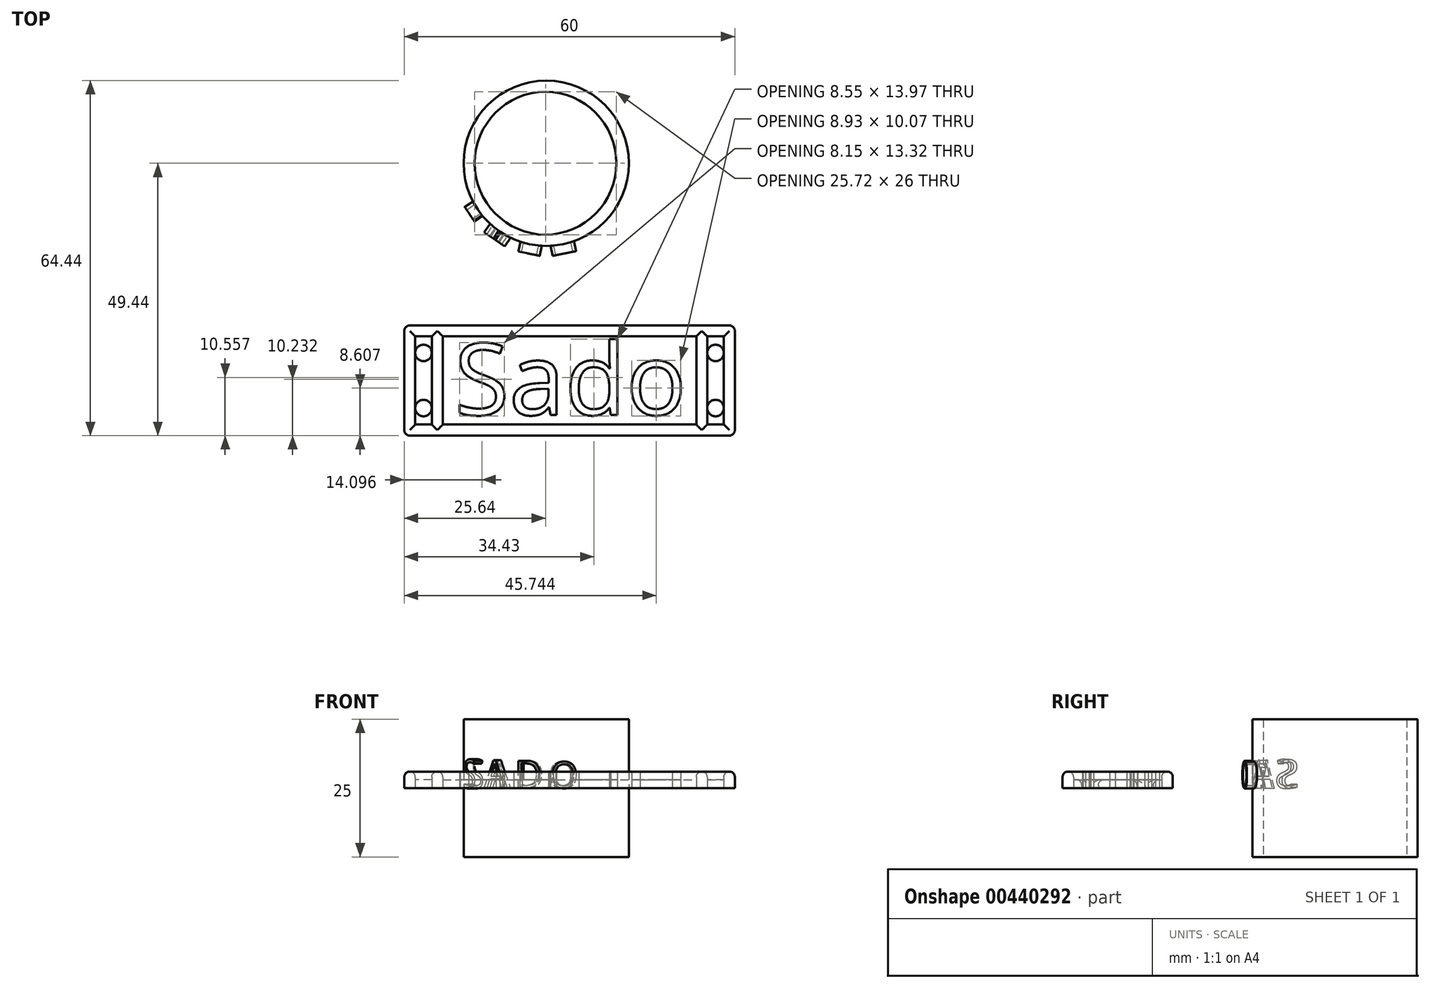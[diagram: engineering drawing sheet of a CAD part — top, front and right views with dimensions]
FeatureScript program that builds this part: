
annotation { "Feature Type Name" : "Feature", "Feature Type Description" : "" }
export const myFeature = defineFeature(function(context is Context, id is Id, definition is map)
    precondition{}
    {
        {
            var Q0;
            Q0=qCreatedBy(makeId("Top.planeOp"),FACE);
            var sketch = newSketch(context, id + "F0", { "sketchPlane" : qUnion([Q0])});
            skLineSegment(sketch, "E0", {"start": v(0, -15) * mm, "end": v(5.74, -13.86) * mm});
            skLineSegment(sketch, "E1", {"start": v(5.74, -13.86) * mm, "end": v(10.6, -10.6) * mm});
            skLineSegment(sketch, "E2", {"start": v(10.6, -10.6) * mm, "end": v(13.86, -5.74) * mm});
            skLineSegment(sketch, "E3", {"start": v(13.86, -5.74) * mm, "end": v(15, 0) * mm});
            skLineSegment(sketch, "E4", {"start": v(15, 0) * mm, "end": v(13.86, 5.74) * mm});
            skLineSegment(sketch, "E5", {"start": v(13.86, 5.74) * mm, "end": v(10.6, 10.6) * mm});
            skLineSegment(sketch, "E6", {"start": v(10.6, 10.6) * mm, "end": v(5.74, 13.86) * mm});
            skLineSegment(sketch, "E7", {"start": v(5.74, 13.86) * mm, "end": v(0, 15) * mm});
            skLineSegment(sketch, "E8", {"start": v(0, 15) * mm, "end": v(-5.74, 13.86) * mm});
            skLineSegment(sketch, "E9", {"start": v(-5.74, 13.86) * mm, "end": v(-10.6, 10.6) * mm});
            skLineSegment(sketch, "E10", {"start": v(-10.6, 10.6) * mm, "end": v(-13.86, 5.74) * mm});
            skLineSegment(sketch, "E11", {"start": v(-13.86, 5.74) * mm, "end": v(-15, 0) * mm});
            skLineSegment(sketch, "E12", {"start": v(-15, 0) * mm, "end": v(-13.86, -5.74) * mm});
            skLineSegment(sketch, "E13", {"start": v(-13.86, -5.74) * mm, "end": v(-10.6, -10.6) * mm});
            skLineSegment(sketch, "E14", {"start": v(-10.6, -10.6) * mm, "end": v(-5.74, -13.86) * mm});
            skLineSegment(sketch, "E15", {"start": v(-5.74, -13.86) * mm, "end": v(0, -15) * mm});
            skSolve(sketch);
        }
        {
            var Q0;
            Q0=qCreatedBy(makeId("Top.planeOp"),FACE);
            var sketch = newSketch(context, id + "F1", { "sketchPlane" : qUnion([Q0])});
            skCircle(sketch, "E16", {"center": v(0, 0) * mm, "radius": 15 * mm});
            skCircle(sketch, "E17.0", {"center": v(0, 0) * mm, "radius": 13 * mm});
            skSolve(sketch);
        }
        {
            var Q0;
            Q0=makeQuery(id+"F0.imprint","IMPRINT",FACE,{"disambiguationData":[TD([[makeQuery(id+"F0.imprint","IMPRINT",EDGE,{"derivedFrom":sQuery(id+"F0.wireOp",EDGE,"E0")}),1.0]])]});
            extrude(context, id + "F2", {"entities" : qUnion([Q0]), "endBound" : BoundingType.SYMMETRIC, "depth" : 25 * mm, "offsetDistance" : 25 * mm});
        }
        {
            var Q0;
            Q0=makeQuery(id+"F2.opExtrude","SWEPT_FACE",FACE,{"disambiguationData":[OSD([sQuery(id+"F0.wireOp",EDGE,"E13")])]});
            var sketch = newSketch(context, id + "F3", { "sketchPlane" : qUnion([Q0])});
            skText(sketch, "E18", { "text": "S", "fontName": "OpenSans-Regular.ttf"});
            const initialGuessF3  = {"E18": [-0.00204, 0, 1, 0, 0.0052]};
            skSetInitialGuess(sketch, initialGuessF3);
            skSolve(sketch);
        }
        {
            var Q0;
            Q0=makeQuery(id+"F3.imprint","IMPRINT",FACE,{"disambiguationData":[TD([[makeQuery(id+"F3.imprint","IMPRINT",EDGE,{"derivedFrom":sQuery(id+"F3.wireOp",EDGE,"E18.sketch_text.stroke-0")}),-1.0]])]});
            extrude(context, id + "F4", {"entities" : qUnion([Q0]), "operationType" : NewBodyOperationType.ADD, "depth" : 2 * mm, "offsetDistance" : 25 * mm});
        }
        {
            var Q0;
            Q0=makeQuery(id+"F2.opExtrude","SWEPT_FACE",FACE,{"disambiguationData":[OSD([sQuery(id+"F0.wireOp",EDGE,"E14")])]});
            var sketch = newSketch(context, id + "F5", { "sketchPlane" : qUnion([Q0])});
            skText(sketch, "E19", { "text": "A", "fontName": "OpenSans-Regular.ttf"});
            skPoint(sketch, "E19.secondSnap0", {"position": v(-0.97, 0) * mm});
            const initialGuessF5  = {"E19": [-0.00237, 0, 1, 0, 0.00511]};
            skSetInitialGuess(sketch, initialGuessF5);
            skSolve(sketch);
        }
        {
            var Q0;
            Q0 = qSketchRegion(id + "F5", true);
            extrude(context, id + "F6", {"entities" : qUnion([Q0]), "operationType" : NewBodyOperationType.ADD, "depth" : 2 * mm, "offsetDistance" : 25 * mm});
        }
        {
            var Q0;
            Q0=makeQuery(id+"F2.opExtrude","SWEPT_FACE",FACE,{"disambiguationData":[OSD([sQuery(id+"F0.wireOp",EDGE,"E15")])]});
            var sketch = newSketch(context, id + "F7", { "sketchPlane" : qUnion([Q0])});
            skText(sketch, "E20", { "text": "D", "fontName": "OpenSans-Regular.ttf"});
            const initialGuessF7  = {"E20": [-0.00251, 0, 1, 0, 0.00501]};
            skSetInitialGuess(sketch, initialGuessF7);
            skSolve(sketch);
        }
        {
            var Q0;
            Q0 = qSketchRegion(id + "F7", true);
            extrude(context, id + "F8", {"entities" : qUnion([Q0]), "operationType" : NewBodyOperationType.ADD, "depth" : 2 * mm, "offsetDistance" : 25 * mm});
        }
        {
            var Q0;
            Q0=makeQuery(id+"F2.opExtrude","SWEPT_FACE",FACE,{"disambiguationData":[OSD([sQuery(id+"F0.wireOp",EDGE,"E0")])]});
            var sketch = newSketch(context, id + "F9", { "sketchPlane" : qUnion([Q0])});
            skText(sketch, "E21", { "text": "O", "fontName": "OpenSans-Regular.ttf"});
            const initialGuessF9  = {"E21": [-0.00258, 0, 1, 0, 0.00478]};
            skSetInitialGuess(sketch, initialGuessF9);
            skSolve(sketch);
        }
        {
            var Q0;
            Q0=makeQuery(id+"F9.imprint","IMPRINT",FACE,{"disambiguationData":[TD([[makeQuery(id+"F9.imprint","IMPRINT",EDGE,{"derivedFrom":sQuery(id+"F9.wireOp",EDGE,"E21.sketch_text.stroke-0")}),-1.0]])]});
            extrude(context, id + "F10", {"entities" : qUnion([Q0]), "operationType" : NewBodyOperationType.ADD, "depth" : 2 * mm, "offsetDistance" : 25 * mm});
        }
        {
            var Q0;
            Q0=makeQuery(id+"F1.imprint","IMPRINT",FACE,{"disambiguationData":[TD([[makeQuery(id+"F1.imprint","IMPRINT",EDGE,{"derivedFrom":sQuery(id+"F1.wireOp",EDGE,"E16")}),1.0]])]});
            extrude(context, id + "F11", {"entities" : qUnion([Q0]), "operationType" : NewBodyOperationType.ADD, "endBound" : BoundingType.SYMMETRIC, "depth" : 25 * mm, "offsetDistance" : 25 * mm});
        }
        {
            var Q0;
            Q0=makeQuery(id+"F11.boolean.opBoolean","MERGE",FACE,{"derivedFrom":[makeQuery(id+"F2.opExtrude","CAP_FACE",FACE,{"disambiguationData":[OSD([sQuery(id+"F0.wireOp",EDGE,"E0"),sQuery(id+"F0.wireOp",EDGE,"E1"),sQuery(id+"F0.wireOp",EDGE,"E2"),sQuery(id+"F0.wireOp",EDGE,"E3"),sQuery(id+"F0.wireOp",EDGE,"E4"),sQuery(id+"F0.wireOp",EDGE,"E5"),sQuery(id+"F0.wireOp",EDGE,"E6"),sQuery(id+"F0.wireOp",EDGE,"E7"),sQuery(id+"F0.wireOp",EDGE,"E8"),sQuery(id+"F0.wireOp",EDGE,"E9"),sQuery(id+"F0.wireOp",EDGE,"E10"),sQuery(id+"F0.wireOp",EDGE,"E11"),sQuery(id+"F0.wireOp",EDGE,"E12"),sQuery(id+"F0.wireOp",EDGE,"E13"),sQuery(id+"F0.wireOp",EDGE,"E14"),sQuery(id+"F0.wireOp",EDGE,"E15")])],"isStart":true}),makeQuery(id+"F11.opExtrude","CAP_FACE",FACE,{"disambiguationData":[OSD([sQuery(id+"F1.wireOp",EDGE,"E16")])],"isStart":true})]});
            var sketch = newSketch(context, id + "F12", { "sketchPlane" : qUnion([Q0])});
            skCircle(sketch, "E22", {"center": v(-0.28, 0) * mm, "radius": 13 * mm});
            skSolve(sketch);
        }
        {
            var Q0;
            Q0=makeQuery(id+"F12.imprint","IMPRINT",FACE,{"disambiguationData":[TD([[makeQuery(id+"F12.imprint","IMPRINT",EDGE,{"derivedFrom":sQuery(id+"F12.wireOp",EDGE,"E22")}),1.0]])]});
            extrude(context, id + "F13", {"entities" : qUnion([Q0]), "operationType" : NewBodyOperationType.REMOVE, "oppositeDirection" : true, "depth" : 70 * mm, "offsetDistance" : 25 * mm});
        }
        {
            var Q0;
            Q0 = qSketchRegion(id + "F1", true);
            extrude(context, id + "F14", {"entities" : qUnion([Q0]), "operationType" : NewBodyOperationType.ADD, "endBound" : BoundingType.SYMMETRIC, "depth" : 25 * mm, "offsetDistance" : 25 * mm});
        }
        {
            var Q0;
            Q0=qCreatedBy(makeId("Top.planeOp"),FACE);
            var sketch = newSketch(context, id + "F15", { "sketchPlane" : qUnion([Q0])});
            skLineSegment(sketch, "E23", {"start": v(-20.78, -29.44) * mm, "end": v(-20.78, -49.44) * mm});
            skLineSegment(sketch, "E24", {"start": v(-20.78, -49.44) * mm, "end": v(29.22, -49.44) * mm});
            skLineSegment(sketch, "E25", {"start": v(29.22, -47.44) * mm, "end": v(29.22, -31.44) * mm});
            skLineSegment(sketch, "E26", {"start": v(29.22, -29.44) * mm, "end": v(-20.78, -29.44) * mm});
            skText(sketch, "E27", { "text": "Sado", "fontName": "OpenSans-Regular.ttf"});
            skLineSegment(sketch, "E28.0", {"start": v(27.22, -47.44) * mm, "end": v(27.22, -31.44) * mm});
            skLineSegment(sketch, "E29.0", {"start": v(27.22, -31.44) * mm, "end": v(-18.78, -31.44) * mm});
            skLineSegment(sketch, "E30.0", {"start": v(-18.78, -47.44) * mm, "end": v(27.22, -47.44) * mm});
            skLineSegment(sketch, "E31.0", {"start": v(-18.78, -31.44) * mm, "end": v(-18.78, -47.44) * mm});
            skLineSegment(sketch, "E32.0", {"start": v(34.22, -49.44) * mm, "end": v(34.22, -29.44) * mm});
            skLineSegment(sketch, "E33", {"start": v(29.22, -49.44) * mm, "end": v(34.22, -49.44) * mm});
            skLineSegment(sketch, "E34", {"start": v(29.22, -29.44) * mm, "end": v(34.22, -29.44) * mm});
            skCircle(sketch, "E35", {"center": v(30.72, -34.44) * mm, "radius": 1.5 * mm});
            skCircle(sketch, "E36.MirrorC", {"center": v(30.72, -44.44) * mm, "radius": 1.5 * mm});
            skLineSegment(sketch, "E37.0", {"start": v(29.22, -31.44) * mm, "end": v(32.22, -31.44) * mm});
            skLineSegment(sketch, "E38.0", {"start": v(29.22, -47.44) * mm, "end": v(32.22, -47.44) * mm});
            skLineSegment(sketch, "E39.0", {"start": v(32.22, -47.44) * mm, "end": v(32.22, -31.44) * mm});
            skLineSegment(sketch, "E40.MirrorCS", {"start": v(-20.78, -31.44) * mm, "end": v(-23.78, -31.44) * mm});
            skLineSegment(sketch, "E41.MirrorCS", {"start": v(-20.78, -47.44) * mm, "end": v(-23.78, -47.44) * mm});
            skCircle(sketch, "E42.MirrorC", {"center": v(-22.28, -34.44) * mm, "radius": 1.5 * mm});
            skCircle(sketch, "E43.MirrorC", {"center": v(-22.28, -44.44) * mm, "radius": 1.5 * mm});
            skLineSegment(sketch, "E44.MirrorCS", {"start": v(-23.78, -47.44) * mm, "end": v(-23.78, -31.44) * mm});
            skLineSegment(sketch, "E45.MirrorCS", {"start": v(-20.78, -49.44) * mm, "end": v(-25.78, -49.44) * mm});
            skLineSegment(sketch, "E46.MirrorCS", {"start": v(-20.78, -29.44) * mm, "end": v(-25.78, -29.44) * mm});
            skLineSegment(sketch, "E47.MirrorCS", {"start": v(-25.78, -49.44) * mm, "end": v(-25.78, -29.44) * mm});
            const initialGuessF15  = {"E27": [-0.0167, -0.04569, 1, 0, 0.01307]};
            skSetInitialGuess(sketch, initialGuessF15);
            skSolve(sketch);
        }
        {
            var Q0;
            Q0 = qSketchRegion(id + "F15", true);
            var Q1;
            Q1=makeQuery(id+"F15.imprint","IMPRINT",FACE,{"disambiguationData":[TD([[makeQuery(id+"F15.imprint","IMPRINT",EDGE,{"derivedFrom":sQuery(id+"F15.wireOp",EDGE,"E27.sketch_text.stroke-76")}),-1.0]])]});
            var Q2;
            Q2=makeQuery(id+"F15.imprint","IMPRINT",FACE,{"disambiguationData":[TD([[makeQuery(id+"F15.imprint","IMPRINT",EDGE,{"derivedFrom":sQuery(id+"F15.wireOp",EDGE,"E27.sketch_text.stroke-52")}),-1.0]])]});
            var Q3;
            Q3=makeQuery(id+"F15.imprint","IMPRINT",FACE,{"disambiguationData":[TD([[makeQuery(id+"F15.imprint","IMPRINT",EDGE,{"derivedFrom":sQuery(id+"F15.wireOp",EDGE,"E27.sketch_text.stroke-25")}),-1.0]])]});
            var Q4;
            Q4=makeQuery(id+"F15.imprint","IMPRINT",FACE,{"disambiguationData":[TD([[makeQuery(id+"F15.imprint","IMPRINT",EDGE,{"derivedFrom":sQuery(id+"F15.wireOp",EDGE,"E27.sketch_text.stroke-0")}),-1.0]])]});
            extrude(context, id + "F16", {"entities" : qUnion([Q0, Q1, Q2, Q3, Q4]), "depth" : 3 * mm, "offsetDistance" : 25 * mm});
        }
        {
            var Q0;
            Q0=makeQuery(id+"F15.imprint","IMPRINT",FACE,{"disambiguationData":[TD([[makeQuery(id+"F15.imprint","IMPRINT",EDGE,{"derivedFrom":sQuery(id+"F15.wireOp",EDGE,"E27.sketch_text.stroke-0")}),1.0]])]});
            var Q1;
            Q1=makeQuery(id+"F15.imprint","IMPRINT",FACE,{"disambiguationData":[TD([[makeQuery(id+"F15.imprint","IMPRINT",EDGE,{"derivedFrom":sQuery(id+"F15.wireOp",EDGE,"E27.sketch_text.stroke-85")}),1.0]])]});
            var Q2;
            {var subQ0=sQuery(id+"F15.wireOp",EDGE,"E36.MirrorC");var subQ1=sQuery(id+"F15.wireOp",EDGE,"E25");var subQ2=makeQuery(id+"F15.imprint","INTERSECT",VERTEX,{"derivedFrom":[subQ1,subQ0]});Q2=makeQuery(id+"F15.imprint","IMPRINT",FACE,{"disambiguationData":[TD([[makeQuery(id+"F15.imprint","IMPRINT",EDGE,{"disambiguationData":[TD([[subQ2,-1.0]])],"derivedFrom":subQ1}),-1.0]])]});}
            var Q3;
            {var subQ0=sQuery(id+"F15.wireOp",EDGE,"E37.0");Q3=makeQuery(id+"F15.imprint","IMPRINT",FACE,{"disambiguationData":[TD([[makeQuery(id+"F15.imprint","IMPRINT",EDGE,{"derivedFrom":subQ0}),-1.0]])]});}
            var Q4;
            {var subQ0=sQuery(id+"F15.wireOp",EDGE,"E38.0");Q4=makeQuery(id+"F15.imprint","IMPRINT",FACE,{"disambiguationData":[TD([[makeQuery(id+"F15.imprint","IMPRINT",EDGE,{"derivedFrom":subQ0}),1.0]])]});}
            var Q5;
            Q5=makeQuery(id+"F15.imprint","IMPRINT",FACE,{"disambiguationData":[TD([[makeQuery(id+"F15.imprint","IMPRINT",EDGE,{"derivedFrom":sQuery(id+"F15.wireOp",EDGE,"E27.sketch_text.stroke-67")}),1.0]])]});
            var Q6;
            Q6=makeQuery(id+"F15.imprint","IMPRINT",FACE,{"disambiguationData":[TD([[makeQuery(id+"F15.imprint","IMPRINT",EDGE,{"derivedFrom":sQuery(id+"F15.wireOp",EDGE,"E27.sketch_text.stroke-44")}),1.0]])]});
            var Q7;
            {var subQ0=sQuery(id+"F15.wireOp",EDGE,"E42.MirrorC");var subQ1=sQuery(id+"F15.wireOp",EDGE,"E23");var subQ2=makeQuery(id+"F15.imprint","INTERSECT",VERTEX,{"derivedFrom":[subQ1,subQ0]});Q7=makeQuery(id+"F15.imprint","IMPRINT",FACE,{"disambiguationData":[TD([[makeQuery(id+"F15.imprint","IMPRINT",EDGE,{"disambiguationData":[TD([[subQ2,-1.0]])],"derivedFrom":subQ1}),-1.0]])]});}
            var Q8;
            {var subQ0=sQuery(id+"F15.wireOp",EDGE,"E40.MirrorCS");Q8=makeQuery(id+"F15.imprint","IMPRINT",FACE,{"disambiguationData":[TD([[makeQuery(id+"F15.imprint","IMPRINT",EDGE,{"derivedFrom":subQ0}),1.0]])]});}
            var Q9;
            {var subQ0=sQuery(id+"F15.wireOp",EDGE,"E41.MirrorCS");Q9=makeQuery(id+"F15.imprint","IMPRINT",FACE,{"disambiguationData":[TD([[makeQuery(id+"F15.imprint","IMPRINT",EDGE,{"derivedFrom":subQ0}),-1.0]])]});}
            extrude(context, id + "F17", {"entities" : qUnion([Q0, Q1, Q2, Q3, Q4, Q5, Q6, Q7, Q8, Q9]), "depth" : 1.5 * mm, "offsetDistance" : 25 * mm});
        }
        {
            var Q0;
            Q0=makeQuery(id+"F16.opExtrude","CAP_FACE",FACE,{"disambiguationData":[OSD([sQuery(id+"F15.wireOp",EDGE,"E23"),sQuery(id+"F15.wireOp",EDGE,"E24"),sQuery(id+"F15.wireOp",EDGE,"E25"),sQuery(id+"F15.wireOp",EDGE,"E26"),sQuery(id+"F15.wireOp",EDGE,"E28.0"),sQuery(id+"F15.wireOp",EDGE,"E29.0"),sQuery(id+"F15.wireOp",EDGE,"E30.0"),sQuery(id+"F15.wireOp",EDGE,"E31.0"),sQuery(id+"F15.wireOp",EDGE,"E32.0"),sQuery(id+"F15.wireOp",EDGE,"E33"),sQuery(id+"F15.wireOp",EDGE,"E34"),sQuery(id+"F15.wireOp",EDGE,"E37.0"),sQuery(id+"F15.wireOp",EDGE,"E38.0"),sQuery(id+"F15.wireOp",EDGE,"E39.0"),sQuery(id+"F15.wireOp",EDGE,"E40.MirrorCS"),sQuery(id+"F15.wireOp",EDGE,"E41.MirrorCS"),sQuery(id+"F15.wireOp",EDGE,"E44.MirrorCS"),sQuery(id+"F15.wireOp",EDGE,"E45.MirrorCS"),sQuery(id+"F15.wireOp",EDGE,"E46.MirrorCS"),sQuery(id+"F15.wireOp",EDGE,"E47.MirrorCS")])],"isStart":false});
            var Q1;
            Q1=makeQuery(id+"F16.opExtrude","SWEPT_EDGE",EDGE,{"disambiguationData":[OSD([sQuery(id+"F15.wireOp",EDGE,"E45.MirrorCS"),sQuery(id+"F15.wireOp",EDGE,"E47.MirrorCS")])]});
            var Q2;
            Q2=makeQuery(id+"F16.opExtrude","SWEPT_EDGE",EDGE,{"disambiguationData":[OSD([sQuery(id+"F15.wireOp",EDGE,"E46.MirrorCS"),sQuery(id+"F15.wireOp",EDGE,"E47.MirrorCS")])]});
            var Q3;
            Q3=makeQuery(id+"F16.opExtrude","SWEPT_EDGE",EDGE,{"disambiguationData":[OSD([sQuery(id+"F15.wireOp",EDGE,"E32.0"),sQuery(id+"F15.wireOp",EDGE,"E34")])]});
            var Q4;
            Q4=makeQuery(id+"F16.opExtrude","SWEPT_EDGE",EDGE,{"disambiguationData":[OSD([sQuery(id+"F15.wireOp",EDGE,"E32.0"),sQuery(id+"F15.wireOp",EDGE,"E33")])]});
            var Q5;
            {var subQ0=sQuery(id+"F15.wireOp",EDGE,"E36.MirrorC");Q5=makeQuery(id+"F17.opExtrude","CAP_EDGE",EDGE,{"disambiguationData":[OSD([subQ0]),TDD([makeQuery(id+"F15.imprint","IMPRINT",EDGE,{"disambiguationData":[TD([[makeQuery(id+"F15.imprint","INTERSECT",VERTEX,{"derivedFrom":[sQuery(id+"F15.wireOp",EDGE,"E25"),subQ0]}),-1.0]])],"derivedFrom":subQ0})])],"isStart":false});}
            var Q6;
            {var subQ0=sQuery(id+"F15.wireOp",EDGE,"E35");Q6=makeQuery(id+"F17.opExtrude","CAP_EDGE",EDGE,{"disambiguationData":[OSD([subQ0]),TDD([makeQuery(id+"F15.imprint","IMPRINT",EDGE,{"disambiguationData":[TD([[makeQuery(id+"F15.imprint","INTERSECT",VERTEX,{"derivedFrom":[sQuery(id+"F15.wireOp",EDGE,"E25"),subQ0]}),-1.0]])],"derivedFrom":subQ0})])],"isStart":false});}
            var Q7;
            {var subQ0=sQuery(id+"F15.wireOp",EDGE,"E35");Q7=makeQuery(id+"F17.opExtrude","CAP_EDGE",EDGE,{"disambiguationData":[OSD([subQ0]),TDD([makeQuery(id+"F15.imprint","IMPRINT",EDGE,{"disambiguationData":[TD([[makeQuery(id+"F15.imprint","INTERSECT",VERTEX,{"derivedFrom":[sQuery(id+"F15.wireOp",EDGE,"E25"),subQ0]}),1.0]])],"derivedFrom":subQ0})])],"isStart":false});}
            var Q8;
            {var subQ0=sQuery(id+"F15.wireOp",EDGE,"E36.MirrorC");Q8=makeQuery(id+"F17.opExtrude","CAP_EDGE",EDGE,{"disambiguationData":[OSD([subQ0]),TDD([makeQuery(id+"F15.imprint","IMPRINT",EDGE,{"disambiguationData":[TD([[makeQuery(id+"F15.imprint","INTERSECT",VERTEX,{"derivedFrom":[sQuery(id+"F15.wireOp",EDGE,"E25"),subQ0]}),1.0]])],"derivedFrom":subQ0})])],"isStart":false});}
            var Q9;
            {var subQ0=sQuery(id+"F15.wireOp",EDGE,"E42.MirrorC");Q9=makeQuery(id+"F17.opExtrude","CAP_EDGE",EDGE,{"disambiguationData":[OSD([subQ0]),TDD([makeQuery(id+"F15.imprint","IMPRINT",EDGE,{"disambiguationData":[TD([[makeQuery(id+"F15.imprint","INTERSECT",VERTEX,{"derivedFrom":[sQuery(id+"F15.wireOp",EDGE,"E23"),subQ0]}),-1.0]])],"derivedFrom":subQ0})])],"isStart":false});}
            var Q10;
            {var subQ0=sQuery(id+"F15.wireOp",EDGE,"E42.MirrorC");Q10=makeQuery(id+"F17.opExtrude","CAP_EDGE",EDGE,{"disambiguationData":[OSD([subQ0]),TDD([makeQuery(id+"F15.imprint","IMPRINT",EDGE,{"disambiguationData":[TD([[makeQuery(id+"F15.imprint","INTERSECT",VERTEX,{"derivedFrom":[sQuery(id+"F15.wireOp",EDGE,"E23"),subQ0]}),1.0]])],"derivedFrom":subQ0})])],"isStart":false});}
            var Q11;
            {var subQ0=sQuery(id+"F15.wireOp",EDGE,"E43.MirrorC");Q11=makeQuery(id+"F17.opExtrude","CAP_EDGE",EDGE,{"disambiguationData":[OSD([subQ0]),TDD([makeQuery(id+"F15.imprint","IMPRINT",EDGE,{"disambiguationData":[TD([[makeQuery(id+"F15.imprint","INTERSECT",VERTEX,{"derivedFrom":[sQuery(id+"F15.wireOp",EDGE,"E23"),subQ0]}),-1.0]])],"derivedFrom":subQ0})])],"isStart":false});}
            var Q12;
            {var subQ0=sQuery(id+"F15.wireOp",EDGE,"E43.MirrorC");Q12=makeQuery(id+"F17.opExtrude","CAP_EDGE",EDGE,{"disambiguationData":[OSD([subQ0]),TDD([makeQuery(id+"F15.imprint","IMPRINT",EDGE,{"disambiguationData":[TD([[makeQuery(id+"F15.imprint","INTERSECT",VERTEX,{"derivedFrom":[sQuery(id+"F15.wireOp",EDGE,"E23"),subQ0]}),1.0]])],"derivedFrom":subQ0})])],"isStart":false});}
            fillet(context, id + "F18", {"entities" : qUnion([Q0, Q1, Q2, Q3, Q4, Q5, Q6, Q7, Q8, Q9, Q10, Q11, Q12]), "radius" : 1 * mm, "tangentPropagation" : true, "allowEdgeOverflow" : false});
        }
    });
